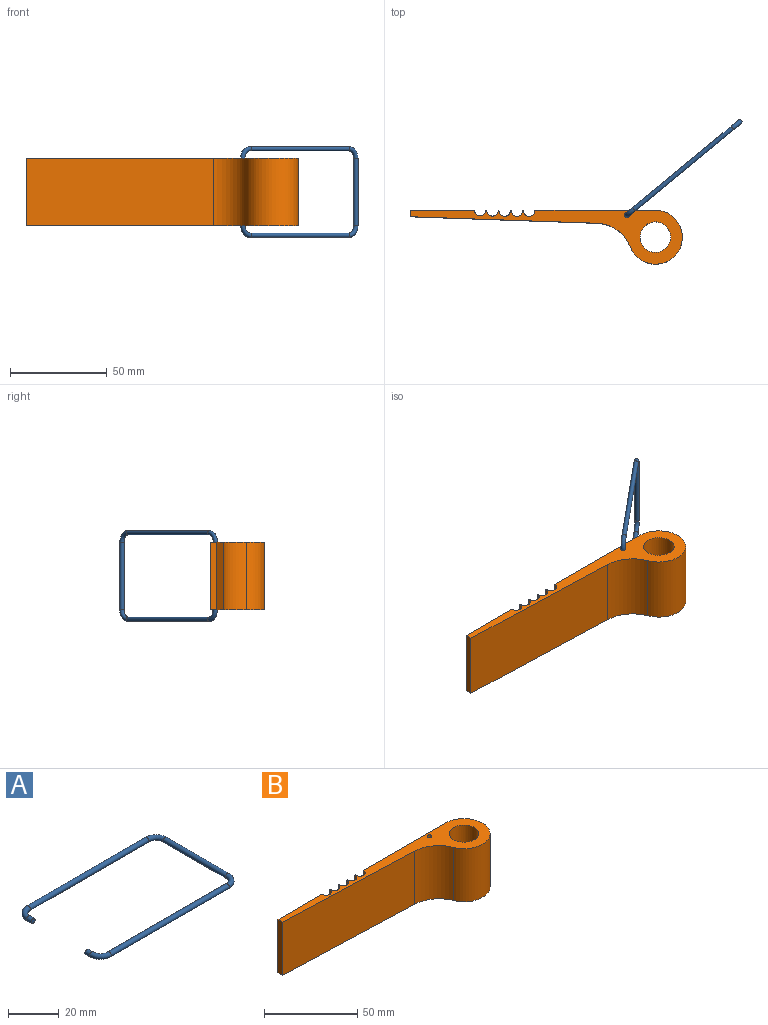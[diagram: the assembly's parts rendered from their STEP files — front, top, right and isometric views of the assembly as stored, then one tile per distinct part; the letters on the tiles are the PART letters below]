
ASSEMBLY  parts=2 mates=1
PART A: 11 faces, bbox 79.2x48.1x2.3 mm
  f0: plane 2.26x2.26mm, normal (0,-1,0), area 4mm2, adj f2
  f1: plane 2.26x2.26mm, normal (0,1,0), area 4mm2, adj f10
  f2: cylinder r=1.13mm len=2.54mm, axis (0,1,0), area 18mm2, adj f0,f3
  f3: torus R=4.97mm, axis (0,0,-1), area 55.4mm2, adj f2,f4
  f4: cylinder r=1.13mm len=66.04mm, axis (1,0,0), area 469mm2, adj f3,f5
  f5: torus R=4.97mm, axis (0,0,-1), area 55.4mm2, adj f4,f6
  f6: cylinder r=1.13mm len=34.87mm, axis (0,-1,0), area 247.7mm2, adj f5,f7
  f7: torus R=4.97mm, axis (0,0,-1), area 55.4mm2, adj f6,f8
  f8: cylinder r=1.13mm len=65.85mm, axis (-1,0,0), area 467.6mm2, adj f7,f9
  f9: torus R=4.97mm, axis (0,0,-1), area 55.4mm2, adj f8,f10
  f10: cylinder r=1.13mm len=2.54mm, axis (0,1,0), area 18mm2, adj f1,f9
PART B: 19 faces, bbox 141x27.9x34.9 mm
  f0: cylinder r=2.97mm len=34.89mm, axis (0,0,-1), area 326mm2, adj f1,f14,f16,f17
  f1: plane 34.89x33.33mm, normal (0,1,0), area 1162.9mm2, adj f0,f2,f16,f17
  f2: plane 34.89x3.4mm, normal (-1,0,0), area 118.5mm2, adj f1,f3,f16,f17
  f3: plane 96.84x34.89mm, normal (-0.03,-1,0), area 3380.5mm2, adj f2,f4,f16,f17
  f4: cylinder r=19.05mm len=34.89mm, axis (0,0,-1), area 776.9mm2, adj f3,f5,f16,f17
  f5: cylinder r=13.97mm len=34.89mm, axis (0,0,-1), area 2118.3mm2, adj f4,f6,f16,f17
  f6: plane 62.33x34.89mm, normal (0,1,0), area 2174.5mm2, adj f5,f7,f16,f17
  f7: cylinder r=2.97mm len=34.89mm, axis (0,0,-1), area 344.7mm2, adj f6,f8,f16,f17
  f8: plane 34.89x0.42mm, normal (0,1,0), area 14.6mm2, adj f7,f9,f16,f17
  f9: cylinder r=2.97mm len=34.89mm, axis (0,0,-1), area 340mm2, adj f8,f10,f16,f17
  f10: plane 34.89x0.41mm, normal (0,1,0), area 14.3mm2, adj f9,f11,f16,f17
  f11: cylinder r=2.97mm len=34.89mm, axis (0,0,-1), area 335.3mm2, adj f10,f12,f16,f17
  f12: plane 34.89x0.4mm, normal (0,1,0), area 14.1mm2, adj f11,f13,f16,f17
  f13: cylinder r=2.97mm len=34.89mm, axis (0,0,-1), area 330.7mm2, adj f12,f14,f16,f17
  f14: plane 34.89x0.4mm, normal (0,1,0), area 14mm2, adj f0,f13,f16,f17
  f15: cylinder r=7.92mm len=34.89mm, axis (0,0,-1), area 1735.8mm2, adj f16,f17
  f16: plane 140.97x27.95mm, normal (0,0,1), area 1031.6mm2, adj f0,f1,f2,f3,f4,f5,f6,f7
  f17: plane 140.97x27.95mm, normal (0,0,-1), area 1031.6mm2, adj f0,f1,f2,f3,f4,f5,f6,f7
  f18: cylinder r=1.27mm len=34.89mm, axis (0,0,-1), area 278.4mm2, adj f16,f17
PLACE A rot(axis=(0.89,0.32,0.32),96.6deg) t=(91.6,22.69,32.94)mm
PLACE B t=(18.6,-19.51,30.4)mm fixed
MATE revolute A.f10 <-> B.f18  axis (0,0,-1) through (54.81,-8.12,30.4)mm
